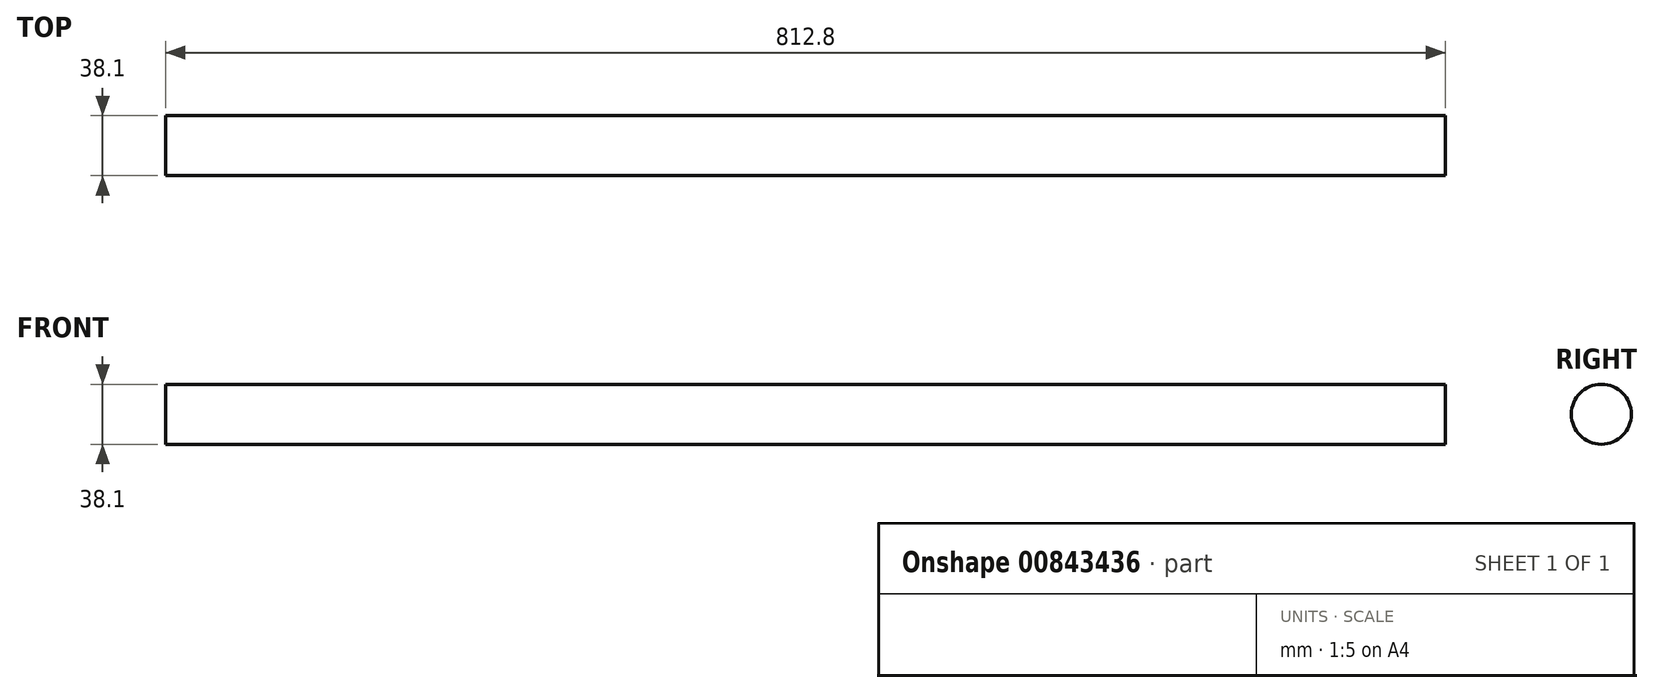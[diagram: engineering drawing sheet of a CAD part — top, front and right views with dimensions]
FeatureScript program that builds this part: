
annotation { "Feature Type Name" : "Feature", "Feature Type Description" : "" }
export const myFeature = defineFeature(function(context is Context, id is Id, definition is map)
    precondition{}
    {
        {
            var Q0;
            Q0=qCreatedBy(makeId("Right.planeOp"),FACE);
            var sketch = newSketch(context, id + "F0", { "sketchPlane" : qUnion([Q0])});
            skCircle(sketch, "E0", {"center": v(0, 0) * mm, "radius": 19.05 * mm});
            skSolve(sketch);
        }
        {
            var Q0;
            Q0=makeQuery(id+"F0.imprint","IMPRINT",FACE,{"disambiguationData":[TD([[makeQuery(id+"F0.imprint","IMPRINT",EDGE,{"derivedFrom":sQuery(id+"F0.wireOp",EDGE,"E0")}),1.0]])]});
            extrude(context, id + "F1", {"entities" : qUnion([Q0]), "depth" : 812.8 * mm, "offsetDistance" : 25.4 * mm});
        }
    });
